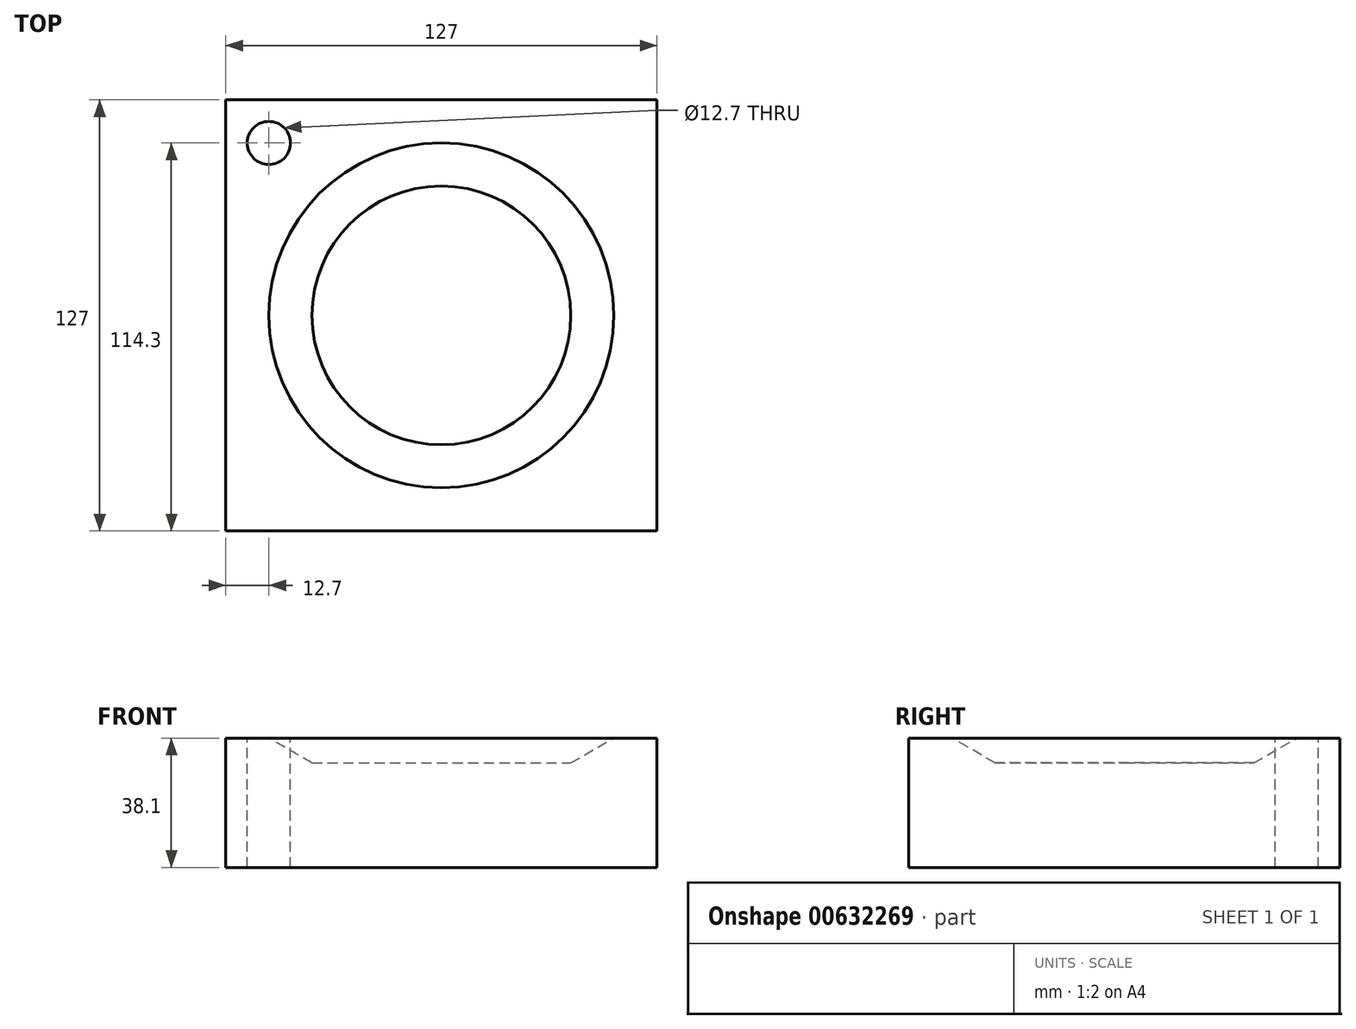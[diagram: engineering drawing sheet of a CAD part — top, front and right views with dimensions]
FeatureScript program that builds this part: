
annotation { "Feature Type Name" : "Feature", "Feature Type Description" : "" }
export const myFeature = defineFeature(function(context is Context, id is Id, definition is map)
    precondition{}
    {
        {
            var Q0;
            Q0=qCreatedBy(makeId("Front.planeOp"),FACE);
            var sketch = newSketch(context, id + "F0", { "sketchPlane" : qUnion([Q0])});
            skLineSegment(sketch, "E0", {"start": v(50.8, 5.8) * mm, "end": v(38.1, -1.52) * mm});
            skLineSegment(sketch, "E1", {"start": v(38.1, -1.52) * mm, "end": v(0, -1.52) * mm});
            skLineSegment(sketch, "E2", {"start": v(50.8, 5.8) * mm, "end": v(0, 5.8) * mm});
            skLineSegment(sketch, "E3", {"start": v(0, 5.8) * mm, "end": v(0, -1.52) * mm});
            skSolve(sketch);
        }
        {
            var Q0;
            Q0=qCreatedBy(makeId("Front.planeOp"),FACE);
            var sketch = newSketch(context, id + "F1", { "sketchPlane" : qUnion([Q0])});
            skLineSegment(sketch, "E4.top", {"start": v(63.5, -32.3) * mm, "end": v(-63.5, -32.3) * mm});
            skLineSegment(sketch, "E4.left", {"start": v(63.5, 5.8) * mm, "end": v(63.5, -32.3) * mm});
            skLineSegment(sketch, "E4.right", {"start": v(-63.5, 5.8) * mm, "end": v(-63.5, -32.3) * mm});
            skLineSegment(sketch, "E5", {"start": v(-63.5, 5.8) * mm, "end": v(0, 5.8) * mm});
            skLineSegment(sketch, "E6", {"start": v(0, 5.8) * mm, "end": v(63.5, 5.8) * mm});
            skSolve(sketch);
        }
        {
            var Q0;
            Q0=qSketchRegion(id+"F1",true);
            extrude(context, id + "F2", {"entities" : qUnion([Q0]), "endBound" : BoundingType.SYMMETRIC, "depth" : 127 * mm, "offsetDistance" : 25.4 * mm});
        }
        {
            var Q0;
            Q0=qSketchRegion(id+"F0",true);
            var Q1;
            Q1=sQuery(id+"F0.wireOp",EDGE,"E3");
            revolve(context, id + "F3", {"operationType" : NewBodyOperationType.REMOVE, "entities" : qUnion([Q0]), "axis" : qUnion([Q1]), "revolveType" : RevolveType.FULL, "oppositeDirection" : true});
        }
        {
            var Q0;
            Q0=qCreatedBy(makeId("Top.planeOp"),FACE);
            var sketch = newSketch(context, id + "F4", { "sketchPlane" : qUnion([Q0])});
            skLineSegment(sketch, "E7", {"start": v(-50.8, 0) * mm, "end": v(-50.8, 50.8) * mm});
            skLineSegment(sketch, "E8", {"start": v(-50.8, 50.8) * mm, "end": v(0, 50.8) * mm});
            skCircle(sketch, "E9", {"center": v(-50.8, 50.8) * mm, "radius": 6.35 * mm});
            skSolve(sketch);
        }
        {
            var Q0;
            Q0 = qSketchRegion(id + "F4", true);
            extrude(context, id + "F5", {"entities" : qUnion([Q0]), "operationType" : NewBodyOperationType.REMOVE, "endBound" : BoundingType.SYMMETRIC, "oppositeDirection" : true, "depth" : 101.6 * mm, "offsetDistance" : 25.4 * mm});
        }
    });
